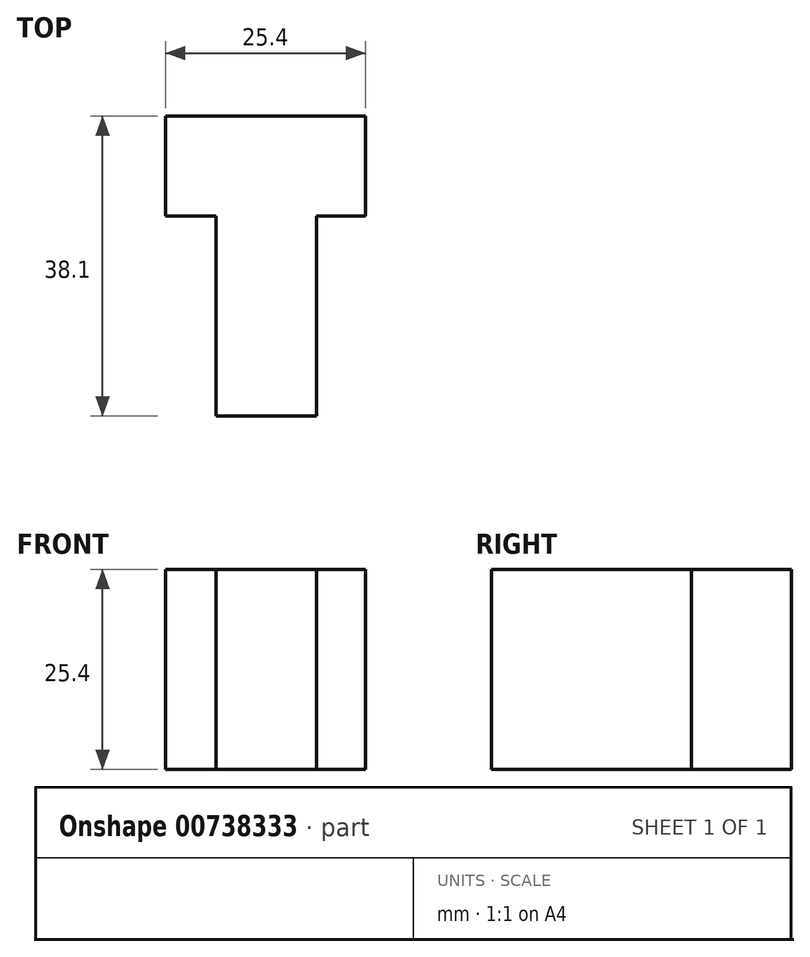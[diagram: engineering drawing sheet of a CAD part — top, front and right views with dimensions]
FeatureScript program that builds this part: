
annotation { "Feature Type Name" : "Feature", "Feature Type Description" : "" }
export const myFeature = defineFeature(function(context is Context, id is Id, definition is map)
    precondition{}
    {
        {
            var Q0;
            Q0=qCreatedBy(makeId("Top.planeOp"),FACE);
            var sketch = newSketch(context, id + "F0", { "sketchPlane" : qUnion([Q0])});
            skLineSegment(sketch, "E0", {"start": v(0, 0) * mm, "end": v(12.74, 0) * mm});
            skLineSegment(sketch, "E1", {"start": v(12.74, 0) * mm, "end": v(12.74, 25.4) * mm});
            skLineSegment(sketch, "E2", {"start": v(12.74, 25.4) * mm, "end": v(18.99, 25.4) * mm});
            skLineSegment(sketch, "E3", {"start": v(18.99, 25.4) * mm, "end": v(18.99, 38.1) * mm});
            skLineSegment(sketch, "E4", {"start": v(18.99, 38.1) * mm, "end": v(-6.41, 38.1) * mm});
            skLineSegment(sketch, "E5", {"start": v(-6.41, 38.1) * mm, "end": v(-6.41, 25.4) * mm});
            skLineSegment(sketch, "E6", {"start": v(-6.41, 25.4) * mm, "end": v(0, 25.4) * mm});
            skLineSegment(sketch, "E7", {"start": v(0, 25.4) * mm, "end": v(0, 0) * mm});
            skSolve(sketch);
        }
        {
            var Q0;
            Q0=makeQuery(id+"F0.imprint","IMPRINT",FACE,{"disambiguationData":[TD([[makeQuery(id+"F0.imprint","IMPRINT",EDGE,{"derivedFrom":sQuery(id+"F0.wireOp",EDGE,"E0")}),1.0]])]});
            extrude(context, id + "F1", {"entities" : qUnion([Q0]), "depth" : 25.4 * mm, "offsetDistance" : 25.4 * mm});
        }
    });
